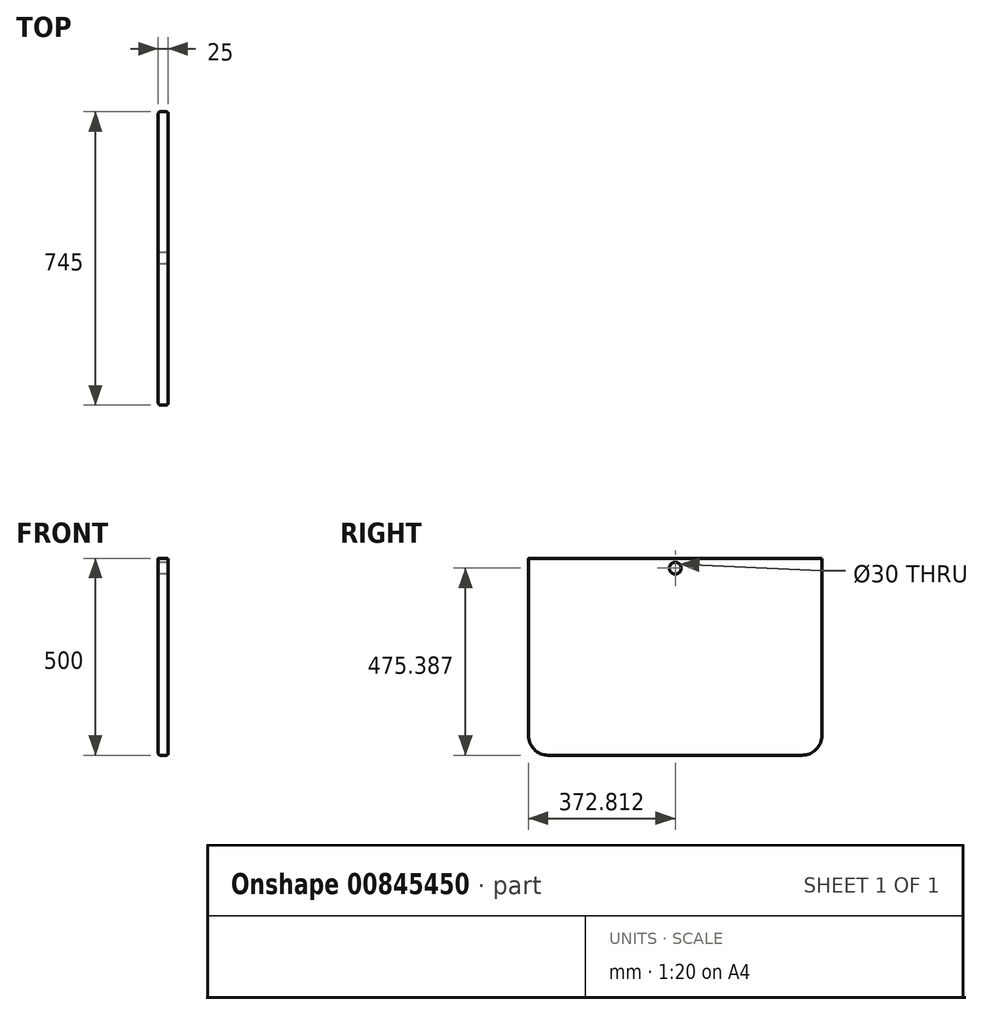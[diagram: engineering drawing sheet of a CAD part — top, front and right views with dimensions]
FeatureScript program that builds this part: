
annotation { "Feature Type Name" : "Feature", "Feature Type Description" : "" }
export const myFeature = defineFeature(function(context is Context, id is Id, definition is map)
    precondition{}
    {
        {
            var Q0;
            Q0=qCreatedBy(makeId("Right.planeOp"),FACE);
            var sketch = newSketch(context, id + "F0", { "sketchPlane" : qUnion([Q0])});
            skLineSegment(sketch, "E0.bottom", {"start": v(-325.93, 227.99) * mm, "end": v(419.07, 227.99) * mm});
            skLineSegment(sketch, "E0.top", {"start": v(-275.93, -272.01) * mm, "end": v(369.07, -272.01) * mm});
            skLineSegment(sketch, "E0.left", {"start": v(-325.93, 227.99) * mm, "end": v(-325.93, -222.01) * mm});
            skLineSegment(sketch, "E0.right", {"start": v(419.07, 227.99) * mm, "end": v(419.07, -222.01) * mm});
            skPoint(sketch, "E1.visualSharp", {"position": v(419.07, -272.01) * mm});
            skArc(sketch, "E1.filletArc", {"start": v(369.07, -272.01) * mm, "mid": v(404.43, -257.37) * mm, "end": v(419.07, -222.01) * mm});
            skPoint(sketch, "E2.visualSharp", {"position": v(-325.93, -272.01) * mm});
            skArc(sketch, "E2.filletArc", {"start": v(-325.93, -222.01) * mm, "mid": v(-311.28, -257.37) * mm, "end": v(-275.93, -272.01) * mm});
            skSolve(sketch);
        }
        {
            var Q0;
            Q0 = qSketchRegion(id + "F0", true);
            extrude(context, id + "F1", {"entities" : qUnion([Q0]), "depth" : 25 * mm, "offsetDistance" : 25 * mm});
        }
        {
            var Q0;
            Q0=makeQuery(id+"F1.opExtrude","CAP_FACE",FACE,{"disambiguationData":[OSD([sQuery(id+"F0.wireOp",EDGE,"E0.bottom"),sQuery(id+"F0.wireOp",EDGE,"E0.top"),sQuery(id+"F0.wireOp",EDGE,"E0.left"),sQuery(id+"F0.wireOp",EDGE,"E0.right"),sQuery(id+"F0.wireOp",EDGE,"E1.filletArc"),sQuery(id+"F0.wireOp",EDGE,"E2.filletArc")])],"isStart":true});
            var sketch = newSketch(context, id + "F2", { "sketchPlane" : qUnion([Q0])});
            skCircle(sketch, "E3", {"center": v(-46.88, 203.38) * mm, "radius": 15 * mm});
            skSolve(sketch);
        }
        {
            var Q0;
            Q0=makeQuery(id+"F2.imprint","IMPRINT",FACE,{"disambiguationData":[TD([[makeQuery(id+"F2.imprint","IMPRINT",EDGE,{"derivedFrom":sQuery(id+"F2.wireOp",EDGE,"E3")}),1.0]])]});
            extrude(context, id + "F3", {"entities" : qUnion([Q0]), "operationType" : NewBodyOperationType.REMOVE, "oppositeDirection" : true, "depth" : 25 * mm, "offsetDistance" : 25 * mm});
        }
        {
            var Q0;
            Q0=makeQuery(id+"F1.opExtrude","CAP_EDGE",EDGE,{"disambiguationData":[OSD([sQuery(id+"F0.wireOp",EDGE,"E0.top")])],"isStart":false});
            var Q1;
            Q1=makeQuery(id+"F1.opExtrude","CAP_EDGE",EDGE,{"disambiguationData":[OSD([sQuery(id+"F0.wireOp",EDGE,"E0.top")])],"isStart":true});
            fillet(context, id + "F4", {"entities" : qUnion([Q0, Q1]), "radius" : 5 * mm, "tangentPropagation" : true, "allowEdgeOverflow" : false});
        }
    });
